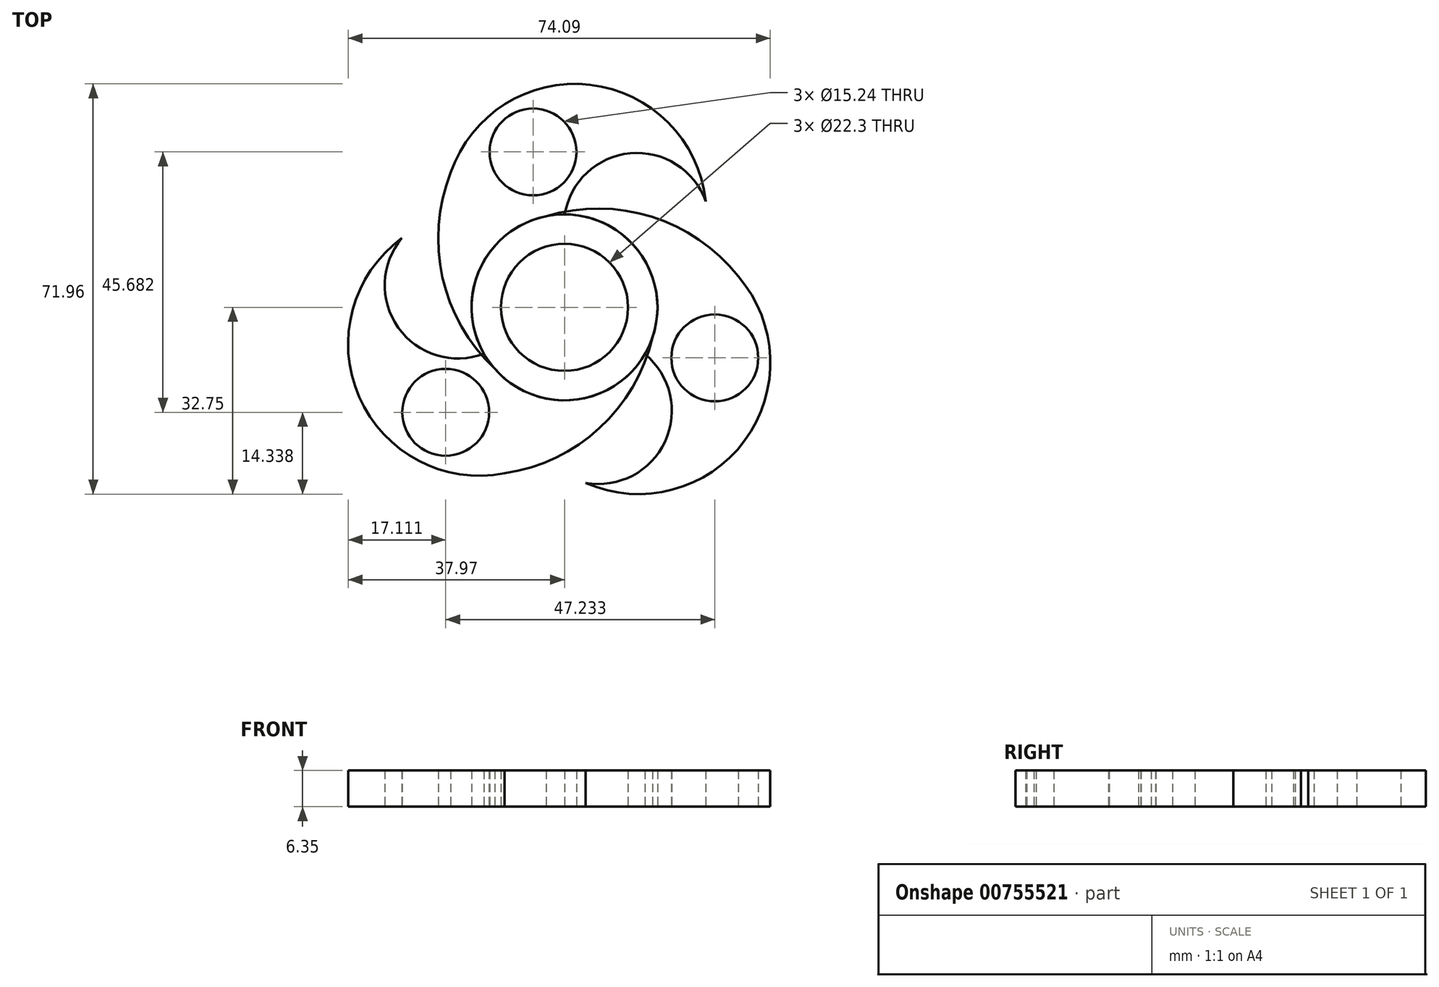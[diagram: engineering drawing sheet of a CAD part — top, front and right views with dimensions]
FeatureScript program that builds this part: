
annotation { "Feature Type Name" : "Feature", "Feature Type Description" : "" }
export const myFeature = defineFeature(function(context is Context, id is Id, definition is map)
    precondition{}
    {
        {
            var Q0;
            Q0=qCreatedBy(makeId("Top.planeOp"),FACE);
            var sketch = newSketch(context, id + "F0", { "sketchPlane" : qUnion([Q0])});
            skCircle(sketch, "E0", {"center": v(0, 0) * mm, "radius": 11.15 * mm});
            skCircle(sketch, "E1", {"center": v(0, 0) * mm, "radius": 12.5 * mm});
            skCircle(sketch, "E2", {"center": v(-5.52, 27.27) * mm, "radius": 7.62 * mm});
            skArc(sketch, "E3", {"start": v(24.8, 18.62) * mm, "mid": v(9.64, 26.72) * mm, "end": v(0, 12.5) * mm});
            skArc(sketch, "E4", {"start": v(24.8, 18.62) * mm, "mid": v(-9.37, 36.3) * mm, "end": v(-12.33, -2.06) * mm});
            skCircle(sketch, "E5", {"center": v(0, 0) * mm, "radius": 16.31 * mm});
            skArc(sketch, "E6", {"start": v(-19.95, 23.68) * mm, "mid": v(-21.41, 5.27) * mm, "end": v(-12.26, -10.76) * mm});
            skCircle(sketch, "E7", {"center": v(0, 0) * mm, "radius": 50.8 * mm, "construction": true});
            skSolve(sketch);
        }
        {
            var Q0;
            Q0=makeQuery(id+"F0.imprint","IMPRINT",FACE,{"disambiguationData":[TD([[makeQuery(id+"F0.imprint","IMPRINT",EDGE,{"derivedFrom":sQuery(id+"F0.wireOp",EDGE,"E2")}),-1.0]])]});
            var Q1;
            Q1=makeQuery(id+"F0.imprint","IMPRINT",FACE,{"disambiguationData":[TD([[makeQuery(id+"F0.imprint","IMPRINT",EDGE,{"derivedFrom":sQuery(id+"F0.wireOp",EDGE,"607143e7-eb06-432f-8de2-a46ea5ccccc6.1.0")}),-1.0]])]});
            var Q2;
            Q2=makeQuery(id+"F0.imprint","IMPRINT",FACE,{"disambiguationData":[TD([[makeQuery(id+"F0.imprint","IMPRINT",EDGE,{"derivedFrom":sQuery(id+"F0.wireOp",EDGE,"E0")}),-1.0]])]});
            var Q3;
            Q3=makeQuery(id+"F0.imprint","IMPRINT",FACE,{"disambiguationData":[TD([[makeQuery(id+"F0.imprint","IMPRINT",EDGE,{"derivedFrom":sQuery(id+"F0.wireOp",EDGE,"607143e7-eb06-432f-8de2-a46ea5ccccc6.2.0")}),-1.0]])]});
            var Q4;
            {var subQ0=sQuery(id+"F0.wireOp",EDGE,"E4");var subQ1=sQuery(id+"F0.wireOp",EDGE,"E1");var subQ2=makeQuery(id+"F0.imprint","INTERSECT",VERTEX,{"derivedFrom":[subQ1,subQ0]});Q4=makeQuery(id+"F0.imprint","IMPRINT",FACE,{"disambiguationData":[TD([[makeQuery(id+"F0.imprint","IMPRINT",EDGE,{"disambiguationData":[TD([[subQ2,-1.0]])],"derivedFrom":subQ1}),-1.0]])]});}
            var Q5;
            {var subQ0=sQuery(id+"F0.wireOp",EDGE,"E3");var subQ1=sQuery(id+"F0.wireOp",EDGE,"E1");var subQ2=makeQuery(id+"F0.imprint","INTERSECT",VERTEX,{"derivedFrom":[subQ1,subQ0]});Q5=makeQuery(id+"F0.imprint","IMPRINT",FACE,{"disambiguationData":[TD([[makeQuery(id+"F0.imprint","IMPRINT",EDGE,{"disambiguationData":[TD([[subQ2,-1.0]])],"derivedFrom":subQ1}),-1.0]])]});}
            var Q6;
            {var subQ0=sQuery(id+"F0.wireOp",EDGE,"E3");var subQ1=sQuery(id+"F0.wireOp",EDGE,"E1");var subQ2=makeQuery(id+"F0.imprint","INTERSECT",VERTEX,{"derivedFrom":[subQ1,subQ0]});Q6=makeQuery(id+"F0.imprint","IMPRINT",FACE,{"disambiguationData":[TD([[makeQuery(id+"F0.imprint","IMPRINT",EDGE,{"disambiguationData":[TD([[subQ2,1.0]])],"derivedFrom":subQ1}),-1.0]])]});}
            var Q7;
            {var subQ0=sQuery(id+"F0.wireOp",EDGE,"607143e7-eb06-432f-8de2-a46ea5ccccc6.2.1");var subQ1=sQuery(id+"F0.wireOp",EDGE,"E1");var subQ2=makeQuery(id+"F0.imprint","INTERSECT",VERTEX,{"derivedFrom":[subQ1,subQ0]});Q7=makeQuery(id+"F0.imprint","IMPRINT",FACE,{"disambiguationData":[TD([[makeQuery(id+"F0.imprint","IMPRINT",EDGE,{"disambiguationData":[TD([[subQ2,1.0]])],"derivedFrom":subQ1}),-1.0]])]});}
            var Q8;
            {var subQ0=sQuery(id+"F0.wireOp",EDGE,"607143e7-eb06-432f-8de2-a46ea5ccccc6.1.1");var subQ1=sQuery(id+"F0.wireOp",EDGE,"E1");var subQ2=makeQuery(id+"F0.imprint","INTERSECT",VERTEX,{"derivedFrom":[subQ1,subQ0]});Q8=makeQuery(id+"F0.imprint","IMPRINT",FACE,{"disambiguationData":[TD([[makeQuery(id+"F0.imprint","IMPRINT",EDGE,{"disambiguationData":[TD([[subQ2,-1.0]])],"derivedFrom":subQ1}),-1.0]])]});}
            var Q9;
            {var subQ0=sQuery(id+"F0.wireOp",EDGE,"607143e7-eb06-432f-8de2-a46ea5ccccc6.1.1");var subQ1=sQuery(id+"F0.wireOp",EDGE,"E1");var subQ2=makeQuery(id+"F0.imprint","INTERSECT",VERTEX,{"derivedFrom":[subQ1,subQ0]});Q9=makeQuery(id+"F0.imprint","IMPRINT",FACE,{"disambiguationData":[TD([[makeQuery(id+"F0.imprint","IMPRINT",EDGE,{"disambiguationData":[TD([[subQ2,1.0]])],"derivedFrom":subQ1}),-1.0]])]});}
            var Q10;
            {var subQ0=sQuery(id+"F0.wireOp",EDGE,"YS9BRsio-8GJt-cjgf-fqPp-NImNVnhpjurN");var subQ1=sQuery(id+"F0.wireOp",EDGE,"E4");var subQ2=makeQuery(id+"F0.imprint","INTERSECT",VERTEX,{"disambiguationData":[OD(1.0)],"derivedFrom":[subQ1,subQ0]});Q10=makeQuery(id+"F0.imprint","IMPRINT",FACE,{"disambiguationData":[TD([[makeQuery(id+"F0.imprint","IMPRINT",EDGE,{"disambiguationData":[TD([[subQ2,-1.0]])],"derivedFrom":subQ1}),-1.0]])]});}
            extrude(context, id + "F1", {"entities" : qUnion([Q0, Q1, Q2, Q3, Q4, Q5, Q6, Q7, Q8, Q9, Q10]), "depth" : 6.35 * mm, "offsetDistance" : 25.4 * mm});
        }
        {
            var Q0;
            Q0=qCreatedBy(makeId("Front.planeOp"),FACE);
            var sketch = newSketch(context, id + "F2", { "sketchPlane" : qUnion([Q0])});
            skLineSegment(sketch, "E8", {"start": v(0, 38.44) * mm, "end": v(0, -15.2) * mm});
            skLineSegment(sketch, "E9", {"start": v(0, -15.2) * mm, "end": v(0, 38.44) * mm});
            skSolve(sketch);
        }
        {
            var Q0;
            Q0=makeQuery(id+"F1.opExtrude","SWEPT_BODY",BODY,{"disambiguationData":[OSD([sQuery(id+"F0.wireOp",EDGE,"E0"),sQuery(id+"F0.wireOp",EDGE,"E1"),sQuery(id+"F0.wireOp",EDGE,"E2"),sQuery(id+"F0.wireOp",EDGE,"E3"),sQuery(id+"F0.wireOp",EDGE,"E4")])]});
            var Q1;
            Q1=sQuery(id+"F2.wireOp",EDGE,"E9");
            circularPattern(context, id + "F3", {"entities" : qUnion([Q0]), "axis" : qUnion([Q1]), "angle" : 360 * degree, "instanceCount" : 3, "equalSpace" : true});
        }
    });
